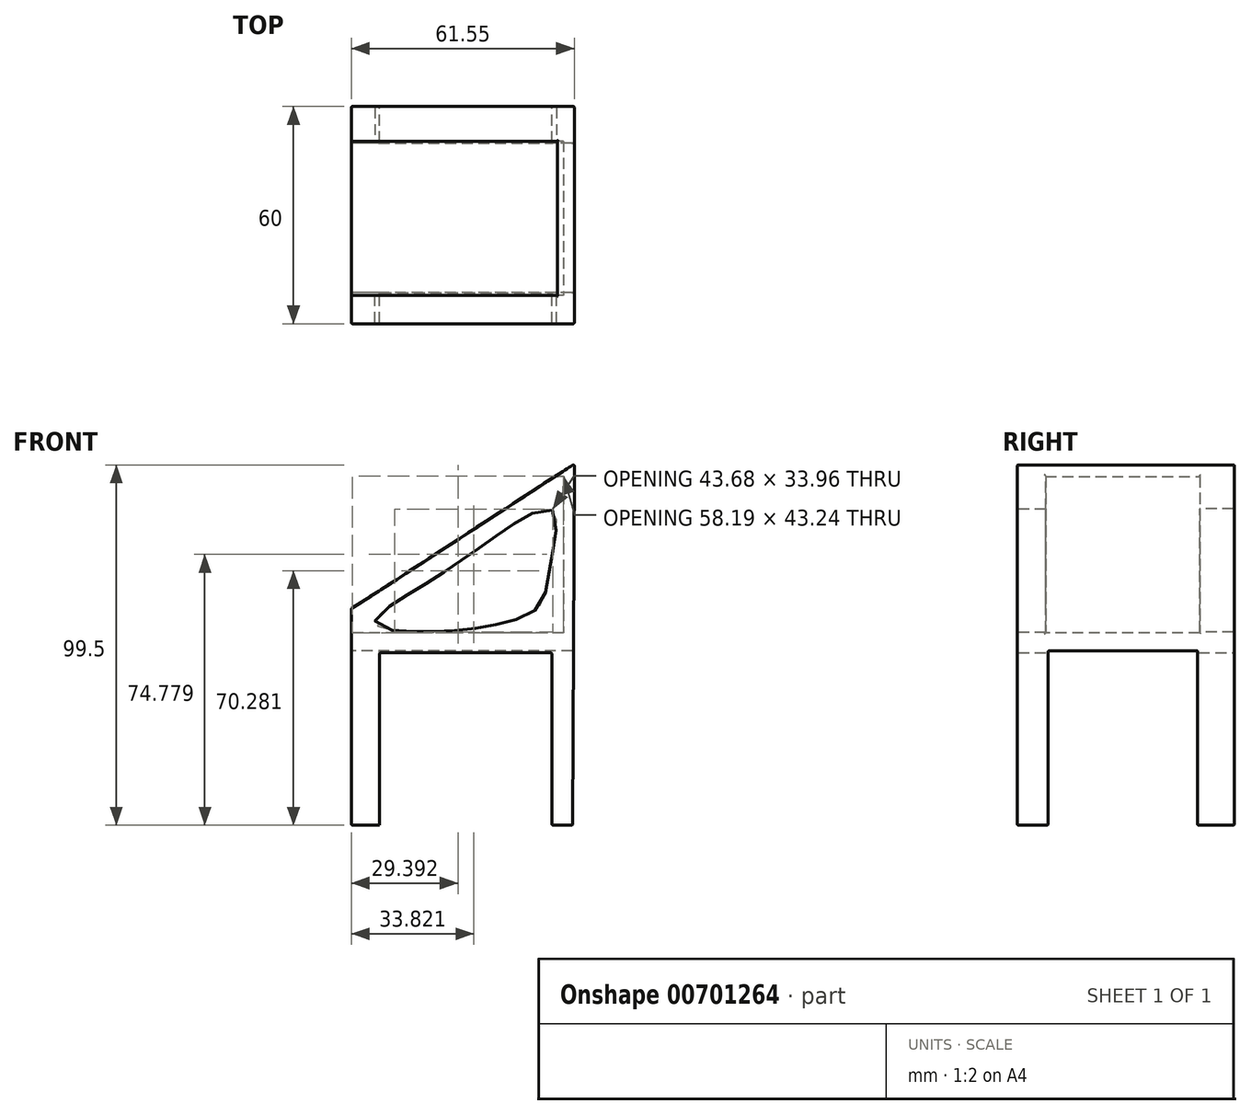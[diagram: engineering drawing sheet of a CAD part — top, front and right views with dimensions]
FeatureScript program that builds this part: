
annotation { "Feature Type Name" : "Feature", "Feature Type Description" : "" }
export const myFeature = defineFeature(function(context is Context, id is Id, definition is map)
    precondition{}
    {
        {
            var Q0;
            Q0=qCreatedBy(makeId("Front.planeOp"),FACE);
            var sketch = newSketch(context, id + "F0", { "sketchPlane" : qUnion([Q0])});
            skFitSpline(sketch, "E0", {"points": [v(20.07, 66.4) * mm, v(-41.48, 26.45) * mm], "startDerivative": vector(-56.4, -36.23) * mm, "endDerivative": vector(-56.4, -36.23) * mm});
            skFitSpline(sketch, "E1", {"points": [v(-41.48, 26.45) * mm, v(-41.48, -33.36) * mm, v(-41.48, -36.95) * mm], "startDerivative": vector(0, -97.3) * mm, "endDerivative": vector(0, -4.04) * mm});
            skFitSpline(sketch, "E2", {"points": [v(-41.48, -33.36) * mm, v(19.64, -33.36) * mm], "startDerivative": vector(63, 0) * mm, "endDerivative": vector(63, 0) * mm});
            skLineSegment(sketch, "E3", {"start": v(20.07, 66.4) * mm, "end": v(19.64, -33.36) * mm});
            skSolve(sketch);
        }
        {
            var Q0;
            Q0 = qSketchRegion(id + "F0", true);
            extrude(context, id + "F1", {"entities" : qUnion([Q0]), "depth" : 60 * mm, "offsetDistance" : 25 * mm});
        }
        {
            var Q0;
            Q0=qCreatedBy(makeId("Front.planeOp"),FACE);
            var sketch = newSketch(context, id + "F2", { "sketchPlane" : qUnion([Q0])});
            skFitSpline(sketch, "E4", {"points": [v(14, 53.66) * mm, v(-16.8, 35.95) * mm, v(-34.54, 21.87) * mm, v(6.48, 24.34) * mm, v(13.06, 36.37) * mm, v(14, 53.66) * mm]});
            skSolve(sketch);
        }
        {
            var Q0;
            Q0 = qSketchRegion(id + "F2", true);
            extrude(context, id + "F3", {"entities" : qUnion([Q0]), "operationType" : NewBodyOperationType.REMOVE, "depth" : 61.2 * mm, "offsetDistance" : 25 * mm});
        }
        {
            var Q0;
            Q0=qCreatedBy(makeId("Top.planeOp"),FACE);
            cPlane(context, id + "F4", {"entities" : qUnion([Q0]), "cplaneType" : CPlaneType.OFFSET, "offset" : 19.8 * mm, "width" : 150 * mm, "height" : 150 * mm});
        }
        {
            var Q0;
            Q0=qCreatedBy(id+"F4.planeOp",FACE);
            var sketch = newSketch(context, id + "F5", { "sketchPlane" : qUnion([Q0])});
            skLineSegment(sketch, "E5.bottom", {"start": v(17, -9.6) * mm, "end": v(-42.02, -9.6) * mm});
            skLineSegment(sketch, "E5.top", {"start": v(17, -52.14) * mm, "end": v(-42.02, -52.14) * mm});
            skLineSegment(sketch, "E5.left", {"start": v(17, -9.6) * mm, "end": v(17, -52.14) * mm});
            skLineSegment(sketch, "E5.right", {"start": v(-42.02, -9.6) * mm, "end": v(-42.02, -52.14) * mm});
            skSolve(sketch);
        }
        {
            var Q0;
            Q0 = qSketchRegion(id + "F5", true);
            extrude(context, id + "F6", {"entities" : qUnion([Q0]), "operationType" : NewBodyOperationType.REMOVE, "depth" : 43.1 * mm, "offsetDistance" : 25 * mm});
        }
        {
            var Q0;
            Q0=makeQuery(id+"F1.opExtrude","CAP_FACE",FACE,{"disambiguationData":[OSD([sQuery(id+"F0.wireOp",EDGE,"E0"),sQuery(id+"F0.wireOp",EDGE,"E1"),sQuery(id+"F0.wireOp",EDGE,"E2"),sQuery(id+"F0.wireOp",EDGE,"29209b33-468f-464b-b479-85e0334b76f1")])],"isStart":true});
            var sketch = newSketch(context, id + "F7", { "sketchPlane" : qUnion([Q0])});
            skLineSegment(sketch, "E6.bottom", {"start": v(-13.86, 14.24) * mm, "end": v(33.7, 14.24) * mm});
            skLineSegment(sketch, "E6.top", {"start": v(-13.86, -43.78) * mm, "end": v(33.7, -43.78) * mm});
            skLineSegment(sketch, "E6.left", {"start": v(-13.86, 14.24) * mm, "end": v(-13.86, -43.78) * mm});
            skLineSegment(sketch, "E6.right", {"start": v(33.7, 14.24) * mm, "end": v(33.7, -43.78) * mm});
            skSolve(sketch);
        }
        {
            var Q0;
            Q0 = qSketchRegion(id + "F7", true);
            extrude(context, id + "F8", {"entities" : qUnion([Q0]), "operationType" : NewBodyOperationType.REMOVE, "oppositeDirection" : true, "depth" : 60 * mm, "offsetDistance" : 25 * mm});
        }
        {
            var Q0;
            Q0=makeQuery(id+"F1.opExtrude","SWEPT_FACE",FACE,{"disambiguationData":[OSD([sQuery(id+"F0.wireOp",EDGE,"E1")])]});
            cPlane(context, id + "F9", {"entities" : qUnion([Q0]), "cplaneType" : CPlaneType.OFFSET, "offset" : 17.1 * mm, "width" : 150 * mm, "height" : 150 * mm});
        }
        {
            var Q0;
            Q0=qCreatedBy(id+"F9.planeOp",FACE);
            var sketch = newSketch(context, id + "F10", { "sketchPlane" : qUnion([Q0])});
            skLineSegment(sketch, "E7.bottom", {"start": v(10.16, 14.85) * mm, "end": v(51.44, 14.85) * mm});
            skLineSegment(sketch, "E7.top", {"start": v(10.16, -36.1) * mm, "end": v(51.44, -36.1) * mm});
            skLineSegment(sketch, "E7.left", {"start": v(10.16, 14.85) * mm, "end": v(10.16, -36.1) * mm});
            skLineSegment(sketch, "E7.right", {"start": v(51.44, 14.85) * mm, "end": v(51.44, -36.1) * mm});
            skSolve(sketch);
        }
        {
            var Q0;
            Q0=makeQuery(id+"F10.imprint","IMPRINT",FACE,{"disambiguationData":[TD([[makeQuery(id+"F10.imprint","IMPRINT",EDGE,{"derivedFrom":sQuery(id+"F10.wireOp",EDGE,"E7.bottom")}),-1.0]])]});
            extrude(context, id + "F11", {"entities" : qUnion([Q0]), "operationType" : NewBodyOperationType.REMOVE, "oppositeDirection" : true, "depth" : 110 * mm, "offsetDistance" : 25 * mm});
        }
        {
            var Q0;
            Q0=makeQuery(id+"F1.opExtrude","SWEPT_FACE",FACE,{"disambiguationData":[OSD([sQuery(id+"F0.wireOp",EDGE,"E0")])]});
            var Q1;
            Q1=makeQuery(id+"F1.opExtrude","SWEPT_FACE",FACE,{"disambiguationData":[OSD([sQuery(id+"F0.wireOp",EDGE,"E1")])]});
            var Q2;
            Q2=makeQuery(id+"F1.opExtrude","CAP_FACE",FACE,{"disambiguationData":[OSD([sQuery(id+"F0.wireOp",EDGE,"E0"),sQuery(id+"F0.wireOp",EDGE,"E1"),sQuery(id+"F0.wireOp",EDGE,"E2"),sQuery(id+"F0.wireOp",EDGE,"E3")])],"isStart":false});
            var Q3;
            Q3=makeQuery(id+"F1.opExtrude","SWEPT_FACE",FACE,{"disambiguationData":[OSD([sQuery(id+"F0.wireOp",EDGE,"E3")])]});
            var Q4;
            Q4=makeQuery(id+"F1.opExtrude","CAP_FACE",FACE,{"disambiguationData":[OSD([sQuery(id+"F0.wireOp",EDGE,"E0"),sQuery(id+"F0.wireOp",EDGE,"E1"),sQuery(id+"F0.wireOp",EDGE,"E2"),sQuery(id+"F0.wireOp",EDGE,"E3")])],"isStart":true});
            var Q5;
            Q5=makeQuery(id+"F11.boolean.opBoolean","COPY",FACE,{"derivedFrom":makeQuery(id+"F11.opExtrude","SWEPT_FACE",FACE,{"disambiguationData":[OSD([sQuery(id+"F10.wireOp",EDGE,"E7.left")])]})});
            var Q6;
            Q6=makeQuery(id+"F11.boolean.opBoolean","SPLIT",FACE,{"disambiguationData":[TD([makeQuery(id+"F11.opExtrude","SWEPT_FACE",FACE,{"disambiguationData":[OSD([sQuery(id+"F10.wireOp",EDGE,"E7.left")])]})])],"derivedFrom":makeQuery(id+"F8.boolean.opBoolean","COPY",FACE,{"derivedFrom":makeQuery(id+"F8.opExtrude","SWEPT_FACE",FACE,{"disambiguationData":[OSD([sQuery(id+"F7.wireOp",EDGE,"E6.left")])]})})});
            var Q7;
            Q7=makeQuery(id+"F11.boolean.opBoolean","COPY",FACE,{"derivedFrom":makeQuery(id+"F11.opExtrude","SWEPT_FACE",FACE,{"disambiguationData":[OSD([sQuery(id+"F10.wireOp",EDGE,"E7.bottom")])]})});
            var Q8;
            Q8=makeQuery(id+"F11.boolean.opBoolean","SPLIT",FACE,{"disambiguationData":[TD([makeQuery(id+"F11.opExtrude","SWEPT_FACE",FACE,{"disambiguationData":[OSD([sQuery(id+"F10.wireOp",EDGE,"E7.right")])]})])],"derivedFrom":makeQuery(id+"F8.boolean.opBoolean","COPY",FACE,{"derivedFrom":makeQuery(id+"F8.opExtrude","SWEPT_FACE",FACE,{"disambiguationData":[OSD([sQuery(id+"F7.wireOp",EDGE,"E6.bottom")])]})})});
            var Q9;
            Q9=makeQuery(id+"F11.boolean.opBoolean","SPLIT",FACE,{"disambiguationData":[TD([makeQuery(id+"F11.opExtrude","SWEPT_FACE",FACE,{"disambiguationData":[OSD([sQuery(id+"F10.wireOp",EDGE,"E7.right")])]})])],"derivedFrom":makeQuery(id+"F8.boolean.opBoolean","COPY",FACE,{"derivedFrom":makeQuery(id+"F8.opExtrude","SWEPT_FACE",FACE,{"disambiguationData":[OSD([sQuery(id+"F7.wireOp",EDGE,"E6.left")])]})})});
            var Q10;
            {var subQ0=sQuery(id+"F0.wireOp",EDGE,"E3");var subQ1=sQuery(id+"F0.wireOp",EDGE,"E2");var subQ5=makeQuery(id+"F1.opExtrude","SWEPT_FACE",FACE,{"disambiguationData":[OSD([subQ0])]});Q10=makeQuery(id+"F11.boolean.opBoolean","SPLIT",FACE,{"disambiguationData":[TD([makeQuery(id+"F11.opExtrude","SWEPT_FACE",FACE,{"disambiguationData":[OSD([sQuery(id+"F10.wireOp",EDGE,"E7.right")])]})])],"derivedFrom":makeQuery(id+"F8.boolean.opBoolean","SPLIT",FACE,{"disambiguationData":[TD([subQ5])],"derivedFrom":makeQuery(id+"F1.opExtrude","SWEPT_FACE",FACE,{"disambiguationData":[OSD([subQ1])]})})});}
            var Q11;
            {var subQ1=sQuery(id+"F0.wireOp",EDGE,"E2");var subQ2=sQuery(id+"F0.wireOp",EDGE,"E1");var subQ5=makeQuery(id+"F1.opExtrude","SWEPT_FACE",FACE,{"disambiguationData":[OSD([subQ2])]});Q11=makeQuery(id+"F11.boolean.opBoolean","SPLIT",FACE,{"disambiguationData":[TD([makeQuery(id+"F11.opExtrude","SWEPT_FACE",FACE,{"disambiguationData":[OSD([sQuery(id+"F10.wireOp",EDGE,"E7.left")])]})])],"derivedFrom":makeQuery(id+"F8.boolean.opBoolean","SPLIT",FACE,{"disambiguationData":[TD([subQ5])],"derivedFrom":makeQuery(id+"F1.opExtrude","SWEPT_FACE",FACE,{"disambiguationData":[OSD([subQ1])]})})});}
            var Q12;
            Q12=makeQuery(id+"F8.boolean.opBoolean","COPY",EDGE,{"derivedFrom":makeQuery(id+"F8.opExtrude","CAP_EDGE",EDGE,{"disambiguationData":[OSD([sQuery(id+"F7.wireOp",EDGE,"E6.right")])],"isStart":false})});
            var Q13;
            Q13=makeQuery(id+"F11.boolean.opBoolean","INTERSECT",EDGE,{"derivedFrom":[makeQuery(id+"F8.boolean.opBoolean","COPY",FACE,{"derivedFrom":makeQuery(id+"F8.opExtrude","SWEPT_FACE",FACE,{"disambiguationData":[OSD([sQuery(id+"F7.wireOp",EDGE,"E6.right")])]})}),makeQuery(id+"F11.opExtrude","SWEPT_FACE",FACE,{"disambiguationData":[OSD([sQuery(id+"F10.wireOp",EDGE,"E7.right")])]})]});
            var Q14;
            {var subQ1=sQuery(id+"F0.wireOp",EDGE,"E2");var subQ2=sQuery(id+"F0.wireOp",EDGE,"E1");Q14=makeQuery(id+"F11.boolean.opBoolean","INTERSECT",EDGE,{"derivedFrom":[makeQuery(id+"F8.boolean.opBoolean","SPLIT",FACE,{"disambiguationData":[TD([makeQuery(id+"F1.opExtrude","SWEPT_FACE",FACE,{"disambiguationData":[OSD([subQ2])]})])],"derivedFrom":makeQuery(id+"F1.opExtrude","SWEPT_FACE",FACE,{"disambiguationData":[OSD([subQ1])]})}),makeQuery(id+"F11.opExtrude","SWEPT_FACE",FACE,{"disambiguationData":[OSD([sQuery(id+"F10.wireOp",EDGE,"E7.right")])]})]});}
            fillet(context, id + "F12", {"entities" : qUnion([Q0, Q1, Q2, Q3, Q4, Q5, Q6, Q7, Q8, Q9, Q10, Q11, Q12, Q13, Q14]), "radius" : 0.3 * mm, "tangentPropagation" : true, "allowEdgeOverflow" : false});
        }
    });
